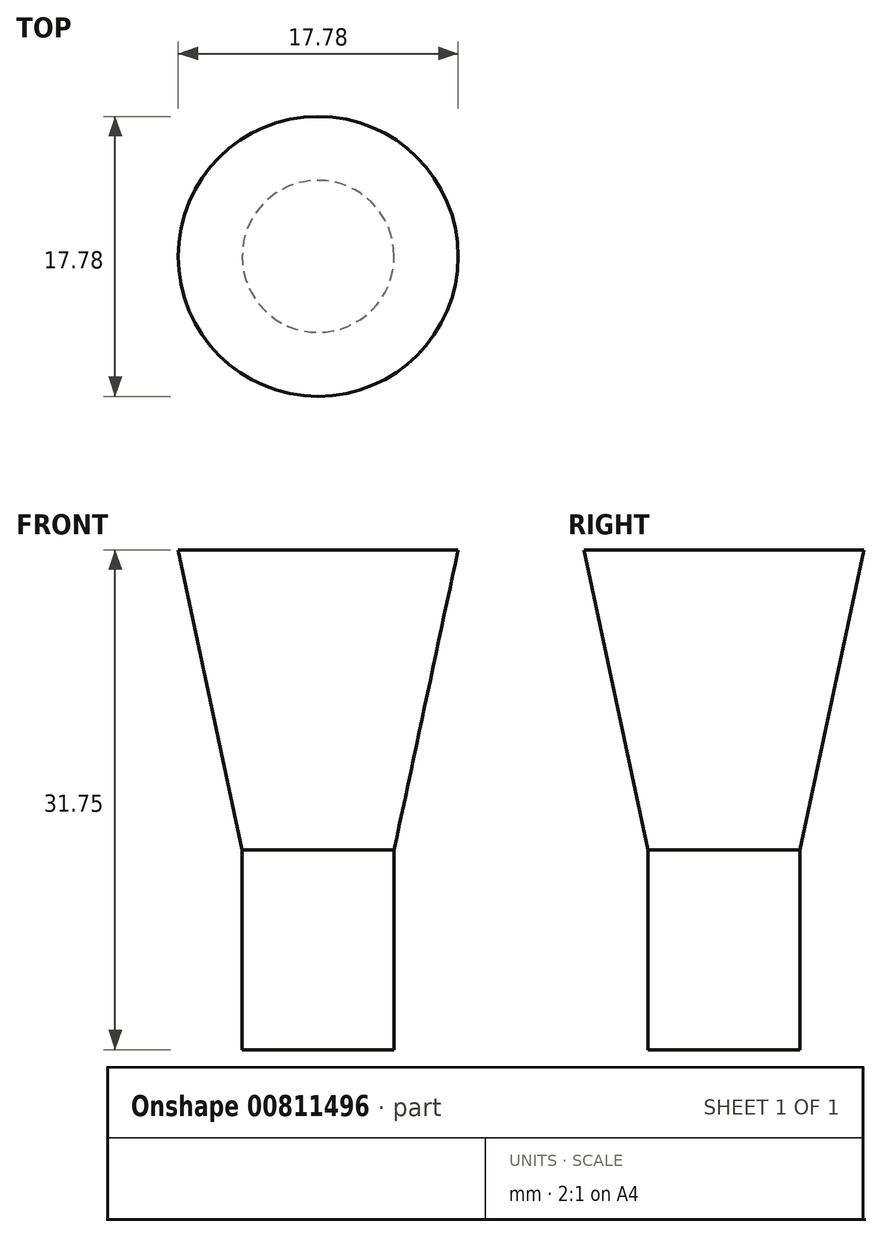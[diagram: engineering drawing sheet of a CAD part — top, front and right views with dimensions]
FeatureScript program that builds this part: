
annotation { "Feature Type Name" : "Feature", "Feature Type Description" : "" }
export const myFeature = defineFeature(function(context is Context, id is Id, definition is map)
    precondition{}
    {
        {
            var Q0;
            Q0=qCreatedBy(makeId("Front.planeOp"),FACE);
            var sketch = newSketch(context, id + "F0", { "sketchPlane" : qUnion([Q0])});
            skLineSegment(sketch, "E0", {"start": v(0, 40.9) * mm, "end": v(0, 21.85) * mm});
            skLineSegment(sketch, "E1", {"start": v(0, 21.85) * mm, "end": v(4.83, 21.85) * mm});
            skLineSegment(sketch, "E2", {"start": v(0, 40.9) * mm, "end": v(8.9, 40.9) * mm});
            skLineSegment(sketch, "E3", {"start": v(8.9, 40.9) * mm, "end": v(4.83, 21.85) * mm});
            skSolve(sketch);
        }
        {
            var Q0;
            Q0=makeQuery(id+"F0.imprint","IMPRINT",FACE,{"disambiguationData":[TD([[makeQuery(id+"F0.imprint","IMPRINT",EDGE,{"derivedFrom":sQuery(id+"F0.wireOp",EDGE,"E0")}),1.0]])]});
            var Q1;
            Q1=sQuery(id+"F0.wireOp",EDGE,"E0");
            revolve(context, id + "F1", {"surfaceOperationType" : NewSurfaceOperationType.NEW, "entities" : qUnion([Q0]), "axis" : qUnion([Q1]), "revolveType" : RevolveType.FULL});
        }
        {
            var Q0;
            Q0=makeQuery(id+"F1.opRevolve","SWEPT_FACE",FACE,{"disambiguationData":[OSD([sQuery(id+"F0.wireOp",EDGE,"E1")])]});
            var sketch = newSketch(context, id + "F2", { "sketchPlane" : qUnion([Q0])});
            skCircle(sketch, "E4", {"center": v(0, 0) * mm, "radius": 4.83 * mm});
            skSolve(sketch);
        }
        {
            var Q0;
            Q0 = qSketchRegion(id + "F2", true);
            extrude(context, id + "F3", {"entities" : qUnion([Q0]), "operationType" : NewBodyOperationType.ADD, "depth" : 12.7 * mm, "offsetDistance" : 25.4 * mm});
        }
    });
